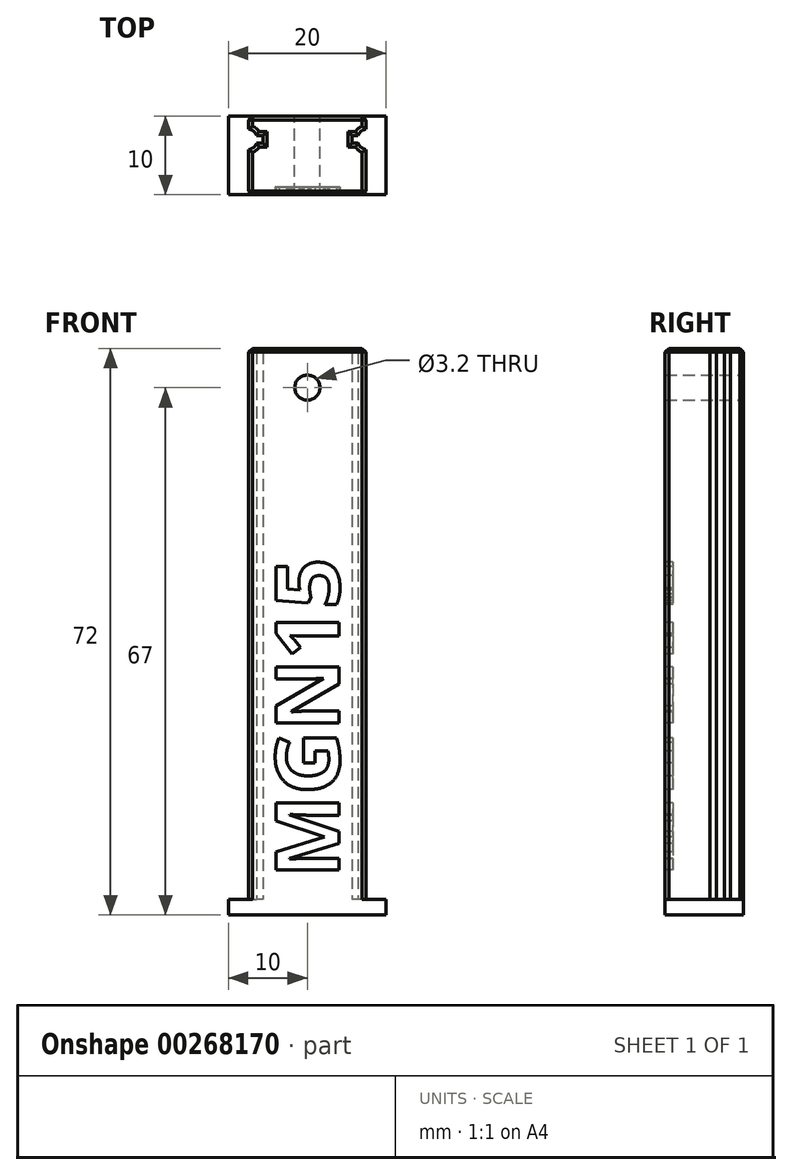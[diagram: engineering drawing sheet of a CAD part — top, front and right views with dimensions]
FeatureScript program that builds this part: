
annotation { "Feature Type Name" : "Feature", "Feature Type Description" : "" }
export const myFeature = defineFeature(function(context is Context, id is Id, definition is map)
    precondition{}
    {
        {
            var Q0;
            Q0=qCreatedBy(makeId("Top.planeOp"),FACE);
            var sketch = newSketch(context, id + "F0", { "sketchPlane" : qUnion([Q0])});
            skLineSegment(sketch, "E0.bottom", {"start": v(10, -5) * mm, "end": v(-10, -5) * mm});
            skLineSegment(sketch, "E0.top", {"start": v(10, 5) * mm, "end": v(-10, 5) * mm});
            skLineSegment(sketch, "E0.left", {"start": v(10, -5) * mm, "end": v(10, 5) * mm});
            skLineSegment(sketch, "E0.right", {"start": v(-10, -5) * mm, "end": v(-10, 5) * mm});
            skPoint(sketch, "E0.middle", {"position": v(0, 0) * mm});
            skSolve(sketch);
        }
        {
            var Q0;
            Q0=qSketchRegion(id+"F0",true);
            extrude(context, id + "F1", {"entities" : qUnion([Q0]), "depth" : 2 * mm});
        }
        {
            var Q0;
            Q0=makeQuery(id+"F1.opExtrude","CAP_FACE",FACE,{"disambiguationData":[OSD([sQuery(id+"F0.wireOp",EDGE,"E0.bottom"),sQuery(id+"F0.wireOp",EDGE,"E0.top"),sQuery(id+"F0.wireOp",EDGE,"E0.left"),sQuery(id+"F0.wireOp",EDGE,"E0.right")])],"isStart":false});
            var sketch = newSketch(context, id + "F2", { "sketchPlane" : qUnion([Q0])});
            skLineSegment(sketch, "E1", {"start": v(-7.45, 5) * mm, "end": v(7.45, 5) * mm});
            skLineSegment(sketch, "E2", {"start": v(-7.45, -5) * mm, "end": v(7.45, -5) * mm});
            skLineSegment(sketch, "E3", {"start": v(7.45, 5) * mm, "end": v(7.45, 3.35) * mm});
            skLineSegment(sketch, "E4", {"start": v(7.45, -5) * mm, "end": v(7.45, 0.75) * mm});
            skLineSegment(sketch, "E5", {"start": v(-7.45, 5) * mm, "end": v(-7.45, 3.35) * mm});
            skLineSegment(sketch, "E6", {"start": v(-7.45, -5) * mm, "end": v(-7.45, 0.75) * mm});
            skLineSegment(sketch, "E7", {"start": v(17.8, 2.05) * mm, "end": v(-22.82, 2.05) * mm, "construction": true});
            skArc(sketch, "E8", {"start": v(7.45, 3.35) * mm, "mid": v(6.85, 3.08) * mm, "end": v(6.45, 2.55) * mm});
            skArc(sketch, "E9", {"start": v(-7.45, 0.75) * mm, "mid": v(-6.85, 1.02) * mm, "end": v(-6.45, 1.55) * mm});
            skPoint(sketch, "E10", {"position": v(7.45, 2.05) * mm});
            skLineSegment(sketch, "E11", {"start": v(-6.45, 2.55) * mm, "end": v(-5.65, 2.55) * mm});
            skLineSegment(sketch, "E12", {"start": v(-5.65, 2.55) * mm, "end": v(-5.65, 1.55) * mm});
            skLineSegment(sketch, "E13", {"start": v(-5.65, 1.55) * mm, "end": v(-6.45, 1.55) * mm});
            skPoint(sketch, "E14", {"position": v(-5.65, 2.05) * mm});
            skArc(sketch, "E15.trimOffspring", {"start": v(-6.45, 2.55) * mm, "mid": v(-6.85, 3.08) * mm, "end": v(-7.45, 3.35) * mm});
            skLineSegment(sketch, "E16", {"start": v(6.45, 2.55) * mm, "end": v(5.65, 2.55) * mm});
            skLineSegment(sketch, "E17", {"start": v(5.65, 2.55) * mm, "end": v(5.65, 1.55) * mm});
            skLineSegment(sketch, "E18", {"start": v(5.65, 1.55) * mm, "end": v(6.45, 1.55) * mm});
            skArc(sketch, "E19.trimOffspring", {"start": v(6.45, 1.55) * mm, "mid": v(6.85, 1.02) * mm, "end": v(7.45, 0.75) * mm});
            skSolve(sketch);
        }
        {
            var Q0;
            Q0=qSketchRegion(id+"F2",true);
            extrude(context, id + "F3", {"entities" : qUnion([Q0]), "operationType" : NewBodyOperationType.ADD, "depth" : 70 * mm});
        }
        {
            var Q0;
            Q0=makeQuery(id+"F3.boolean.opBoolean","MERGE",FACE,{"derivedFrom":[makeQuery(id+"F1.opExtrude","SWEPT_FACE",FACE,{"disambiguationData":[OSD([sQuery(id+"F0.wireOp",EDGE,"E0.top")])]}),makeQuery(id+"F3.opExtrude","SWEPT_FACE",FACE,{"disambiguationData":[OSD([sQuery(id+"F2.wireOp",EDGE,"E1")])]})]});
            var sketch = newSketch(context, id + "F4", { "sketchPlane" : qUnion([Q0])});
            skCircle(sketch, "E20", {"center": v(0, 67) * mm, "radius": 1.6 * mm});
            skSolve(sketch);
        }
        {
            var Q0;
            Q0=qSketchRegion(id+"F4",true);
            extrude(context, id + "F5", {"entities" : qUnion([Q0]), "operationType" : NewBodyOperationType.REMOVE, "endBound" : BoundingType.THROUGH_ALL, "oppositeDirection" : true, "depth" : 25 * mm});
        }
        {
            var Q0;
            Q0=makeQuery(id+"F3.opExtrude","CAP_FACE",FACE,{"disambiguationData":[OSD([sQuery(id+"F2.wireOp",EDGE,"E1"),sQuery(id+"F2.wireOp",EDGE,"E2"),sQuery(id+"F2.wireOp",EDGE,"E3"),sQuery(id+"F2.wireOp",EDGE,"E4"),sQuery(id+"F2.wireOp",EDGE,"E5"),sQuery(id+"F2.wireOp",EDGE,"E6"),sQuery(id+"F2.wireOp",EDGE,"E8"),sQuery(id+"F2.wireOp",EDGE,"E9")])],"isStart":false});
            var Q1;
            Q1=makeQuery(id+"F3.opExtrude","SWEPT_EDGE",EDGE,{"disambiguationData":[OSD([sQuery(id+"F0.wireOp",EDGE,"E0.top"),sQuery(id+"F2.wireOp",EDGE,"E1"),sQuery(id+"F2.wireOp",EDGE,"E5")])]});
            var Q2;
            Q2=makeQuery(id+"F3.opExtrude","SWEPT_EDGE",EDGE,{"disambiguationData":[OSD([sQuery(id+"F0.wireOp",EDGE,"E0.top"),sQuery(id+"F2.wireOp",EDGE,"E1"),sQuery(id+"F2.wireOp",EDGE,"E3")])]});
            var Q3;
            Q3=makeQuery(id+"F3.opExtrude","SWEPT_EDGE",EDGE,{"disambiguationData":[OSD([sQuery(id+"F0.wireOp",EDGE,"E0.bottom"),sQuery(id+"F2.wireOp",EDGE,"E2"),sQuery(id+"F2.wireOp",EDGE,"E6")])]});
            var Q4;
            Q4=makeQuery(id+"F3.opExtrude","SWEPT_EDGE",EDGE,{"disambiguationData":[OSD([sQuery(id+"F0.wireOp",EDGE,"E0.bottom"),sQuery(id+"F2.wireOp",EDGE,"E2"),sQuery(id+"F2.wireOp",EDGE,"E4")])]});
            chamfer(context, id + "F6", {"entities" : qUnion([Q0, Q1, Q2, Q3, Q4]), "width" : .5 * mm, "tangentPropagation" : true});
        }
        {
            var Q0;
            Q0=makeQuery(id+"F3.boolean.opBoolean","MERGE",FACE,{"derivedFrom":[makeQuery(id+"F1.opExtrude","SWEPT_FACE",FACE,{"disambiguationData":[OSD([sQuery(id+"F0.wireOp",EDGE,"E0.bottom")])]}),makeQuery(id+"F3.opExtrude","SWEPT_FACE",FACE,{"disambiguationData":[OSD([sQuery(id+"F2.wireOp",EDGE,"E2")])]})]});
            var sketch = newSketch(context, id + "F7", { "sketchPlane" : qUnion([Q0])});
            skText(sketch, "E21", { "text": "MGN15", "fontName": "OpenSans-Bold.ttf"});
            skPoint(sketch, "E22", {"position": v(0, 45.57) * mm});
            const initialGuessF7  = {"E21": [0.00404, 0.0047, 0, 1, 0.00808]};
            skSetInitialGuess(sketch, initialGuessF7);
            skSolve(sketch);
        }
        {
            var Q0;
            Q0=qSketchRegion(id+"F7",true);
            extrude(context, id + "F8", {"entities" : qUnion([Q0]), "operationType" : NewBodyOperationType.REMOVE, "oppositeDirection" : true, "depth" : 1 * mm});
        }
    });
